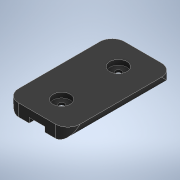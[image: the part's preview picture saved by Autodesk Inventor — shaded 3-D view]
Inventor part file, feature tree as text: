
AUTODESK INVENTOR PART (.ipt)
format: ipt  version: 2021 (Build 250183000, 183)  size: 139,776 bytes
history: native  units: mm
features: extrude x3, sketch x3, fillet x1
ambient origin geometry x8: Origin, YZ Plane, XZ Plane, XY Plane, X Axis, Y Axis, Z Axis, Center Point
bodies: Solid1 (feature_tree)
feature tree (7):
  extrude  "Extrusion1"  Depth=2.0mm
  extrude  "Extrusion2"  Depth=5.0mm
  extrude  "Extrusion3"  Depth=2.5mm
  fillet  "Fillet1"  Radius=2.5mm
  sketch  "Sketch1"  dims[d0=3.2mm d1=2.0mm]
  sketch  "Sketch2"  dims[d2=9.3mm d3=5.0mm]
  sketch  "Sketch3"  dims[d4=43.0mm d5=0.0mm d6=2.5mm d7=2.5mm d8=10.0mm d9=10.0mm d10=43.0mm d11=0.0mm d12=7.0mm d13=7.0mm d14=2.0mm d15=0.0mm d16=5.0mm]
